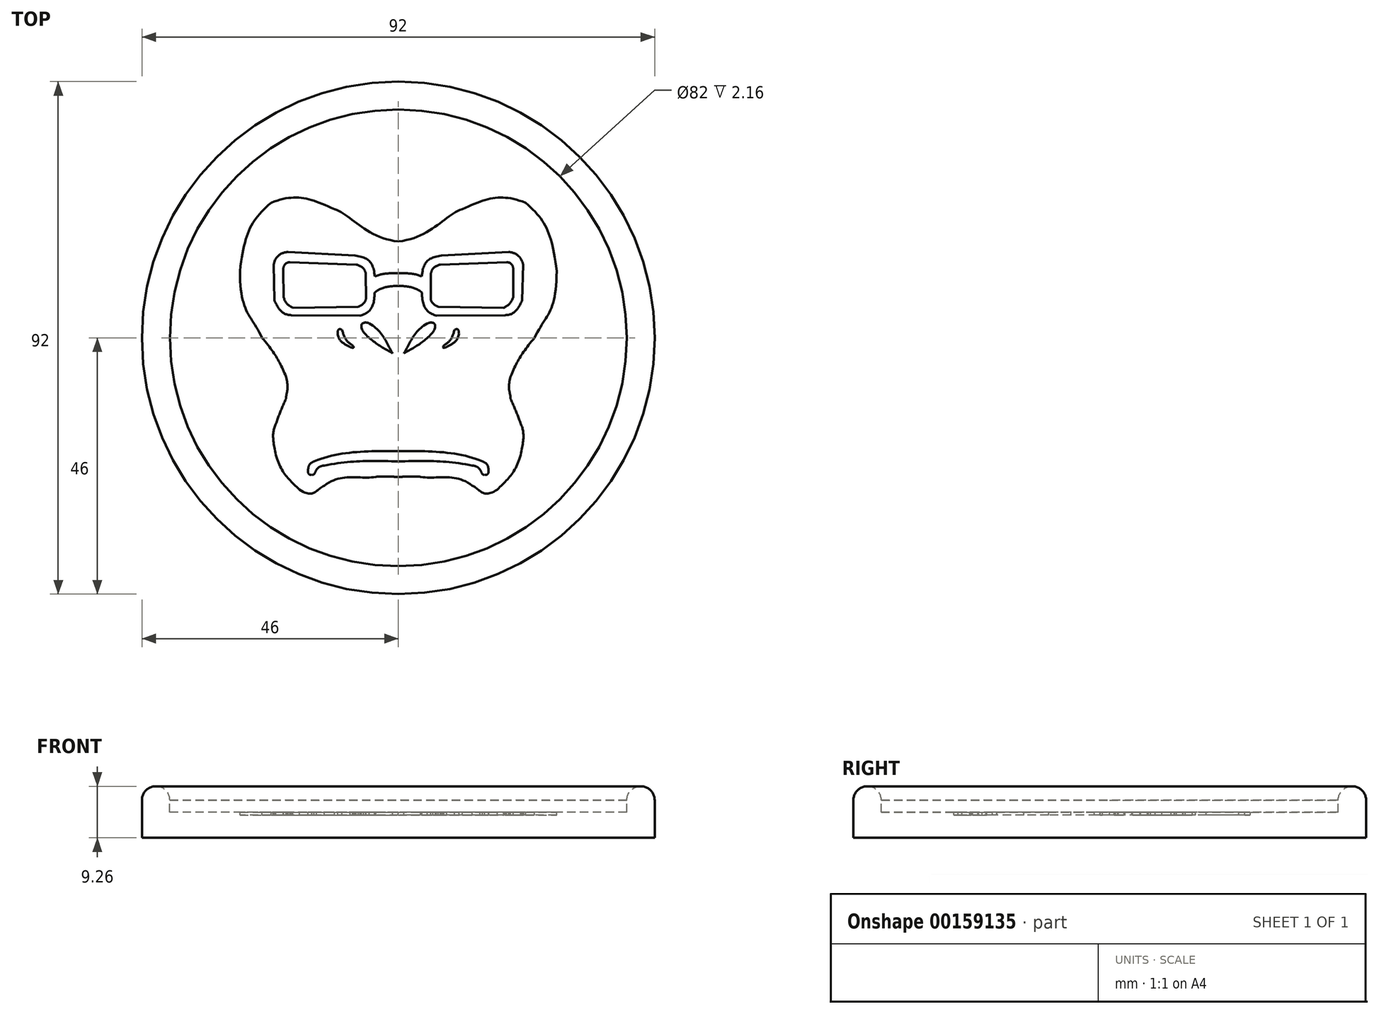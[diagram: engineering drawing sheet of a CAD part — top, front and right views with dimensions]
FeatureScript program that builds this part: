
annotation { "Feature Type Name" : "Feature", "Feature Type Description" : "" }
export const myFeature = defineFeature(function(context is Context, id is Id, definition is map)
    precondition{}
    {
        {
            var Q0;
            Q0=qCreatedBy(makeId("Top.planeOp"),FACE);
            var sketch = newSketch(context, id + "F0", { "sketchPlane" : qUnion([Q0])});
            skCircle(sketch, "E0", {"center": v(0, 0) * mm, "radius": 46 * mm});
            skSolve(sketch);
        }
        {
            var Q0;
            Q0 = qSketchRegion(id + "F0", true);
            extrude(context, id + "F1", {"entities" : qUnion([Q0]), "depth" : 4.6 * mm});
        }
        {
            var Q0;
            Q0=makeQuery(id+"F1.opExtrude","CAP_FACE",FACE,{"disambiguationData":[OSD([sQuery(id+"F0.wireOp",EDGE,"E0")])],"isStart":false});
            var sketch = newSketch(context, id + "F2", { "sketchPlane" : qUnion([Q0])});
            skCircle(sketch, "E1", {"center": v(0, 0) * mm, "radius": 41 * mm});
            skSolve(sketch);
        }
        {
            var Q0;
            Q0 = qSketchRegion(id + "F2", true);
            extrude(context, id + "F3", {"entities" : qUnion([Q0]), "operationType" : NewBodyOperationType.REMOVE, "oppositeDirection" : true, "depth" : 2.16 * mm});
        }
        {
            var Q0;
            Q0=makeQuery(id+"F3.boolean.opBoolean","COPY",FACE,{"derivedFrom":makeQuery(id+"F3.opExtrude","CAP_FACE",FACE,{"disambiguationData":[OSD([sQuery(id+"F2.wireOp",EDGE,"E1")])],"isStart":false})});
            var sketch = newSketch(context, id + "F4", { "sketchPlane" : qUnion([Q0])});
            skFitSpline(sketch, "E2", {"points": [v(-22.82, 24.26) * mm, v(-11.46, 23.12) * mm], "startDerivative": vector(13.27, 5.25) * mm, "endDerivative": vector(13.73, -6.02) * mm});
            skFitSpline(sketch, "E3", {"points": [v(-11.46, 23.12) * mm, v(0, 17.31) * mm], "startDerivative": vector(8.95, -2.93) * mm, "endDerivative": vector(17.4, -1.85) * mm});
            skFitSpline(sketch, "E4", {"points": [v(-22.82, 24.26) * mm, v(-28.41, 12) * mm], "startDerivative": vector(-11.27, -9.64) * mm, "endDerivative": vector(-2.55, -20.44) * mm});
            skFitSpline(sketch, "E5", {"points": [v(-28.41, 12) * mm, v(-24.46, 0) * mm], "startDerivative": vector(0, -22.56) * mm, "endDerivative": vector(6.05, -12.77) * mm});
            skFitSpline(sketch, "E6", {"points": [v(-24.46, 0) * mm, v(-20.15, -6.97) * mm], "startDerivative": vector(6.87, -7.99) * mm, "endDerivative": vector(3.27, -8.01) * mm});
            skFitSpline(sketch, "E7", {"points": [v(-20.15, -6.97) * mm, v(-20.15, -10.95) * mm], "startDerivative": vector(1.96, -7.52) * mm, "endDerivative": vector(0, -4.03) * mm});
            skFitSpline(sketch, "E8", {"points": [v(-20.15, -10.95) * mm, v(-21.95, -15.41) * mm], "startDerivative": vector(-2.02, -4.58) * mm, "endDerivative": vector(-1.63, -5.07) * mm});
            skFitSpline(sketch, "E9", {"points": [v(-21.95, -15.41) * mm, v(-21.95, -21.03) * mm], "startDerivative": vector(-2.13, -4.25) * mm, "endDerivative": vector(1.96, -8.66) * mm});
            skFitSpline(sketch, "E10", {"points": [v(-21.95, -21.03) * mm, v(-17.75, -27.24) * mm], "startDerivative": vector(2.29, -9) * mm, "endDerivative": vector(5.72, -5.56) * mm});
            skFitSpline(sketch, "E11", {"points": [v(-17.75, -27.24) * mm, v(-13.28, -26.53) * mm], "startDerivative": vector(8.01, -5.07) * mm, "endDerivative": vector(4.9, 2.29) * mm});
            skFitSpline(sketch, "E12", {"points": [v(-13.28, -26.53) * mm, v(-4.02, -24.95) * mm], "startDerivative": vector(9.65, 7.36) * mm, "endDerivative": vector(9.26, 1.58) * mm});
            skFitSpline(sketch, "E13", {"points": [v(-4.02, -24.95) * mm, v(0, -24.95) * mm], "startDerivative": vector(4.74, 0.5) * mm, "endDerivative": vector(4.02, 0) * mm});
            skLineSegment(sketch, "E14", {"start": v(0, -24.95) * mm, "end": v(0, 17.31) * mm});
            skFitSpline(sketch, "E15", {"points": [v(0, 11.64) * mm, v(-4.21, 11.03) * mm], "startDerivative": vector(-4.33, -0.13) * mm, "endDerivative": vector(-4.41, -1.82) * mm});
            skFitSpline(sketch, "E16", {"points": [v(-4.26, 8.14) * mm, v(0, 9.35) * mm], "startDerivative": vector(3.63, 2.98) * mm, "endDerivative": vector(5.11, 0.26) * mm});
            skFitSpline(sketch, "E17", {"points": [v(-4.26, 8.14) * mm, v(-6.85, 3.98) * mm], "startDerivative": vector(0, -7.66) * mm, "endDerivative": vector(-5.45, -1.56) * mm});
            skLineSegment(sketch, "E18", {"start": v(-19.18, 4.07) * mm, "end": v(-6.85, 3.98) * mm});
            skFitSpline(sketch, "E19", {"points": [v(-4.21, 11.03) * mm, v(-7.76, 14.8) * mm], "startDerivative": vector(-0.78, 7.79) * mm, "endDerivative": vector(-7.4, 1.17) * mm});
            skLineSegment(sketch, "E20", {"start": v(-19.78, 15.4) * mm, "end": v(-7.76, 14.8) * mm});
            skFitSpline(sketch, "E21", {"points": [v(-22.38, 13.11) * mm, v(-19.78, 15.4) * mm], "startDerivative": vector(1.04, 6.23) * mm, "endDerivative": vector(1.43, 0) * mm});
            skFitSpline(sketch, "E22", {"points": [v(-19.18, 4.07) * mm, v(-22.25, 6.8) * mm], "startDerivative": vector(-4.67, 0.26) * mm, "endDerivative": vector(-2.6, 5.84) * mm});
            skLineSegment(sketch, "E23", {"start": v(-22.38, 13.11) * mm, "end": v(-22.25, 6.8) * mm});
            skFitSpline(sketch, "E24", {"points": [v(-20.65, 12.12) * mm, v(-19.44, 13.59) * mm], "startDerivative": vector(0, 1.17) * mm, "endDerivative": vector(3.37, 0) * mm});
            skFitSpline(sketch, "E25", {"points": [v(-20.6, 7.32) * mm, v(-18.92, 5.41) * mm], "startDerivative": vector(1.43, -3.76) * mm, "endDerivative": vector(2.47, -1.3) * mm});
            skFitSpline(sketch, "E26", {"points": [v(-7.2, 5.59) * mm, v(-5.81, 6.97) * mm], "startDerivative": vector(1.95, 0.65) * mm, "endDerivative": vector(0.39, 2.08) * mm});
            skFitSpline(sketch, "E27", {"points": [v(-7.54, 13.15) * mm, v(-5.86, 11.6) * mm], "startDerivative": vector(3.63, -1.04) * mm, "endDerivative": vector(0.52, -2.2) * mm});
            skLineSegment(sketch, "E28", {"start": v(-19.44, 13.59) * mm, "end": v(-7.54, 13.15) * mm});
            skLineSegment(sketch, "E29", {"start": v(-5.81, 6.97) * mm, "end": v(-5.86, 11.6) * mm});
            skLineSegment(sketch, "E30", {"start": v(-7.2, 5.59) * mm, "end": v(-18.92, 5.41) * mm});
            skLineSegment(sketch, "E31", {"start": v(-20.6, 7.32) * mm, "end": v(-20.65, 12.12) * mm});
            skFitSpline(sketch, "E32", {"points": [v(-14.65, -23.65) * mm, v(-15.49, -24.62) * mm], "startDerivative": vector(-0.84, -0.97) * mm, "endDerivative": vector(-1.65, -0.1) * mm});
            skFitSpline(sketch, "E33", {"points": [v(-15.49, -24.62) * mm, v(-16.17, -23.55) * mm], "startDerivative": vector(-2.24, 0.1) * mm, "endDerivative": vector(0.2, 2.07) * mm});
            skFitSpline(sketch, "E34", {"points": [v(-16.17, -23.55) * mm, v(-15.1, -22.16) * mm], "startDerivative": vector(0.2, 3.01) * mm, "endDerivative": vector(1.56, 0.87) * mm});
            skFitSpline(sketch, "E35", {"points": [v(0, -20.31) * mm, v(-15.1, -22.16) * mm], "startDerivative": vector(-15.46, 0.1) * mm, "endDerivative": vector(-13.6, -5.64) * mm});
            skFitSpline(sketch, "E36", {"points": [v(-14.65, -23.65) * mm, v(-13.29, -22.9) * mm], "startDerivative": vector(0.87, 1.36) * mm, "endDerivative": vector(1.85, 0.2) * mm});
            skFitSpline(sketch, "E37", {"points": [v(-13.29, -22.9) * mm, v(0, -22.2) * mm], "startDerivative": vector(14.29, 2.72) * mm, "endDerivative": vector(14.29, -0.58) * mm});
            skFitSpline(sketch, "E38", {"points": [v(-10.9, 0.78) * mm, v(-8.67, -1.65) * mm], "startDerivative": vector(0.98, -5.13) * mm, "endDerivative": vector(3.27, -2.18) * mm});
            skFitSpline(sketch, "E39", {"points": [v(-10.9, 0.78) * mm, v(-10.1, 1.44) * mm], "startDerivative": vector(0.1, 2.5) * mm, "endDerivative": vector(1.53, -0.87) * mm});
            skFitSpline(sketch, "E40", {"points": [v(-10.1, 1.44) * mm, v(-8.2, -1.33) * mm], "startDerivative": vector(1.3, -4.31) * mm, "endDerivative": vector(3.82, -2.3) * mm});
            skFitSpline(sketch, "E41", {"points": [v(-8.67, -1.65) * mm, v(-8.2, -1.33) * mm], "startDerivative": vector(2.3, -0.87) * mm, "endDerivative": vector(-0.87, 0.98) * mm});
            skFitSpline(sketch, "E42", {"points": [v(-6.24, 1.04) * mm, v(-5.18, 2.56) * mm], "startDerivative": vector(-3.27, 5.24) * mm, "endDerivative": vector(1.96, -1.3) * mm});
            skFitSpline(sketch, "E43", {"points": [v(-5.18, 2.56) * mm, v(-1, -2.78) * mm], "startDerivative": vector(7.42, -3.93) * mm, "endDerivative": vector(3.06, -4.8) * mm});
            skFitSpline(sketch, "E44", {"points": [v(-6.24, 1.04) * mm, v(-1, -2.78) * mm], "startDerivative": vector(5.13, -5.78) * mm, "endDerivative": vector(5.46, -3.16) * mm});
            skFitSpline(sketch, "E45.MirrorCS", {"points": [v(4.21, 11.03) * mm, v(7.76, 14.8) * mm], "startDerivative": vector(0.78, 7.79) * mm, "endDerivative": vector(7.4, 1.17) * mm});
            skFitSpline(sketch, "E46.MirrorCS", {"points": [v(0, 11.64) * mm, v(4.21, 11.03) * mm], "startDerivative": vector(4.33, -0.13) * mm, "endDerivative": vector(4.41, -1.82) * mm});
            skFitSpline(sketch, "E47.MirrorCS", {"points": [v(4.26, 8.14) * mm, v(0, 9.35) * mm], "startDerivative": vector(-3.63, 2.98) * mm, "endDerivative": vector(-5.11, 0.26) * mm});
            skLineSegment(sketch, "E48.MirrorCS", {"start": v(19.78, 15.4) * mm, "end": v(7.76, 14.8) * mm});
            skFitSpline(sketch, "E49.MirrorCS", {"points": [v(22.38, 13.11) * mm, v(19.78, 15.4) * mm], "startDerivative": vector(-1.04, 6.23) * mm, "endDerivative": vector(-1.43, 0) * mm});
            skFitSpline(sketch, "E50.MirrorCS", {"points": [v(19.18, 4.07) * mm, v(22.25, 6.8) * mm], "startDerivative": vector(4.67, 0.26) * mm, "endDerivative": vector(2.6, 5.84) * mm});
            skLineSegment(sketch, "E51.MirrorCS", {"start": v(19.18, 4.07) * mm, "end": v(6.85, 3.98) * mm});
            skLineSegment(sketch, "E52.MirrorCS", {"start": v(22.38, 13.11) * mm, "end": v(22.25, 6.8) * mm});
            skFitSpline(sketch, "E53.MirrorCS", {"points": [v(4.26, 8.14) * mm, v(6.85, 3.98) * mm], "startDerivative": vector(0, -7.66) * mm, "endDerivative": vector(5.45, -1.56) * mm});
            skLineSegment(sketch, "E54.MirrorCS", {"start": v(19.44, 13.59) * mm, "end": v(7.54, 13.15) * mm});
            skFitSpline(sketch, "E55.MirrorCS", {"points": [v(7.54, 13.15) * mm, v(5.86, 11.6) * mm], "startDerivative": vector(-3.63, -1.04) * mm, "endDerivative": vector(-0.52, -2.2) * mm});
            skLineSegment(sketch, "E56.MirrorCS", {"start": v(5.81, 6.97) * mm, "end": v(5.86, 11.6) * mm});
            skLineSegment(sketch, "E57.MirrorCS", {"start": v(7.2, 5.59) * mm, "end": v(18.92, 5.41) * mm});
            skLineSegment(sketch, "E58.MirrorCS", {"start": v(20.6, 7.32) * mm, "end": v(20.65, 12.12) * mm});
            skFitSpline(sketch, "E59.MirrorCS", {"points": [v(20.6, 7.32) * mm, v(18.92, 5.41) * mm], "startDerivative": vector(-1.43, -3.76) * mm, "endDerivative": vector(-2.47, -1.3) * mm});
            skFitSpline(sketch, "E60.MirrorCS", {"points": [v(7.2, 5.59) * mm, v(5.81, 6.97) * mm], "startDerivative": vector(-1.95, 0.65) * mm, "endDerivative": vector(-0.39, 2.08) * mm});
            skFitSpline(sketch, "E61.MirrorCS", {"points": [v(20.65, 12.12) * mm, v(19.44, 13.59) * mm], "startDerivative": vector(0, 1.17) * mm, "endDerivative": vector(-3.37, 0) * mm});
            skFitSpline(sketch, "E62.MirrorCS", {"points": [v(6.24, 1.04) * mm, v(5.18, 2.56) * mm], "startDerivative": vector(3.27, 5.24) * mm, "endDerivative": vector(-1.96, -1.3) * mm});
            skFitSpline(sketch, "E63.MirrorCS", {"points": [v(5.18, 2.56) * mm, v(1, -2.78) * mm], "startDerivative": vector(-7.42, -3.93) * mm, "endDerivative": vector(-3.06, -4.8) * mm});
            skFitSpline(sketch, "E64.MirrorCS", {"points": [v(6.24, 1.04) * mm, v(1, -2.78) * mm], "startDerivative": vector(-5.13, -5.78) * mm, "endDerivative": vector(-5.46, -3.16) * mm});
            skFitSpline(sketch, "E65.MirrorCS", {"points": [v(10.9, 0.78) * mm, v(10.1, 1.44) * mm], "startDerivative": vector(-0.1, 2.5) * mm, "endDerivative": vector(-1.53, -0.87) * mm});
            skFitSpline(sketch, "E66.MirrorCS", {"points": [v(10.9, 0.78) * mm, v(8.67, -1.65) * mm], "startDerivative": vector(-0.98, -5.13) * mm, "endDerivative": vector(-3.27, -2.18) * mm});
            skFitSpline(sketch, "E67.MirrorCS", {"points": [v(10.1, 1.44) * mm, v(8.2, -1.33) * mm], "startDerivative": vector(-1.3, -4.31) * mm, "endDerivative": vector(-3.82, -2.3) * mm});
            skFitSpline(sketch, "E68.MirrorCS", {"points": [v(8.67, -1.65) * mm, v(8.2, -1.33) * mm], "startDerivative": vector(-2.3, -0.87) * mm, "endDerivative": vector(0.87, 0.98) * mm});
            skFitSpline(sketch, "E69.MirrorCS", {"points": [v(22.82, 24.26) * mm, v(11.46, 23.12) * mm], "startDerivative": vector(-13.27, 5.25) * mm, "endDerivative": vector(-13.73, -6.02) * mm});
            skFitSpline(sketch, "E70.MirrorCS", {"points": [v(22.82, 24.26) * mm, v(28.41, 12) * mm], "startDerivative": vector(11.27, -9.64) * mm, "endDerivative": vector(2.55, -20.44) * mm});
            skFitSpline(sketch, "E71.MirrorCS", {"points": [v(11.46, 23.12) * mm, v(0, 17.31) * mm], "startDerivative": vector(-8.95, -2.93) * mm, "endDerivative": vector(-17.4, -1.85) * mm});
            skFitSpline(sketch, "E72.MirrorCS", {"points": [v(28.41, 12) * mm, v(24.46, 0) * mm], "startDerivative": vector(0, -22.56) * mm, "endDerivative": vector(-6.05, -12.77) * mm});
            skFitSpline(sketch, "E73.MirrorCS", {"points": [v(24.46, 0) * mm, v(20.15, -6.97) * mm], "startDerivative": vector(-6.87, -7.99) * mm, "endDerivative": vector(-3.27, -8.01) * mm});
            skFitSpline(sketch, "E74.MirrorCS", {"points": [v(20.15, -6.97) * mm, v(20.15, -10.95) * mm], "startDerivative": vector(-1.96, -7.52) * mm, "endDerivative": vector(0, -4.03) * mm});
            skFitSpline(sketch, "E75.MirrorCS", {"points": [v(20.15, -10.95) * mm, v(21.95, -15.41) * mm], "startDerivative": vector(2.02, -4.58) * mm, "endDerivative": vector(1.63, -5.07) * mm});
            skFitSpline(sketch, "E76.MirrorCS", {"points": [v(21.95, -15.41) * mm, v(21.95, -21.03) * mm], "startDerivative": vector(2.13, -4.25) * mm, "endDerivative": vector(-1.96, -8.66) * mm});
            skFitSpline(sketch, "E77.MirrorCS", {"points": [v(21.95, -21.03) * mm, v(17.75, -27.24) * mm], "startDerivative": vector(-2.29, -9) * mm, "endDerivative": vector(-5.72, -5.56) * mm});
            skFitSpline(sketch, "E78.MirrorCS", {"points": [v(17.75, -27.24) * mm, v(13.28, -26.53) * mm], "startDerivative": vector(-8.01, -5.07) * mm, "endDerivative": vector(-4.9, 2.29) * mm});
            skFitSpline(sketch, "E79.MirrorCS", {"points": [v(13.28, -26.53) * mm, v(4.02, -24.95) * mm], "startDerivative": vector(-9.65, 7.36) * mm, "endDerivative": vector(-9.26, 1.58) * mm});
            skFitSpline(sketch, "E80.MirrorCS", {"points": [v(4.02, -24.95) * mm, v(0, -24.95) * mm], "startDerivative": vector(-4.74, 0.5) * mm, "endDerivative": vector(-4.02, 0) * mm});
            skFitSpline(sketch, "E81.MirrorCS", {"points": [v(13.29, -22.9) * mm, v(0, -22.2) * mm], "startDerivative": vector(-14.29, 2.72) * mm, "endDerivative": vector(-14.29, -0.58) * mm});
            skFitSpline(sketch, "E82.MirrorCS", {"points": [v(0, -20.31) * mm, v(15.1, -22.16) * mm], "startDerivative": vector(15.46, 0.1) * mm, "endDerivative": vector(13.6, -5.64) * mm});
            skFitSpline(sketch, "E83.MirrorCS", {"points": [v(16.17, -23.55) * mm, v(15.1, -22.16) * mm], "startDerivative": vector(-0.2, 3.01) * mm, "endDerivative": vector(-1.56, 0.87) * mm});
            skFitSpline(sketch, "E84.MirrorCS", {"points": [v(15.49, -24.62) * mm, v(16.17, -23.55) * mm], "startDerivative": vector(2.24, 0.1) * mm, "endDerivative": vector(-0.2, 2.07) * mm});
            skFitSpline(sketch, "E85.MirrorCS", {"points": [v(14.65, -23.65) * mm, v(15.49, -24.62) * mm], "startDerivative": vector(0.84, -0.97) * mm, "endDerivative": vector(1.65, -0.1) * mm});
            skFitSpline(sketch, "E86.MirrorCS", {"points": [v(14.65, -23.65) * mm, v(13.29, -22.9) * mm], "startDerivative": vector(-0.87, 1.36) * mm, "endDerivative": vector(-1.85, 0.2) * mm});
            skSolve(sketch);
        }
        {
            var Q0;
            Q0 = qSketchRegion(id + "F4", true);
            var Q1;
            Q1=makeQuery(id+"F4.imprint","IMPRINT",FACE,{"disambiguationData":[TD([[makeQuery(id+"F4.imprint","IMPRINT",EDGE,{"derivedFrom":sQuery(id+"F4.wireOp",EDGE,"E24")}),-1.0]])]});
            var Q2;
            Q2=makeQuery(id+"F4.imprint","IMPRINT",FACE,{"disambiguationData":[TD([[makeQuery(id+"F4.imprint","IMPRINT",EDGE,{"derivedFrom":sQuery(id+"F4.wireOp",EDGE,"E54.MirrorCS")}),1.0]])]});
            extrude(context, id + "F5", {"entities" : qUnion([Q0, Q1, Q2]), "operationType" : NewBodyOperationType.REMOVE, "oppositeDirection" : true, "depth" : .5 * mm});
        }
        {
            var Q0;
            Q0=makeQuery(id+"F1.opExtrude","CAP_FACE",FACE,{"disambiguationData":[OSD([sQuery(id+"F0.wireOp",EDGE,"E0")])],"isStart":true});
            var sketch = newSketch(context, id + "F6", { "sketchPlane" : qUnion([Q0])});
            skCircle(sketch, "E87", {"center": v(0, 0) * mm, "radius": 46 * mm});
            skSolve(sketch);
        }
        {
            var Q0;
            Q0 = qSketchRegion(id + "F6", true);
            extrude(context, id + "F7", {"entities" : qUnion([Q0]), "operationType" : NewBodyOperationType.ADD, "depth" : 2.16 * mm});
        }
        {
            var Q0;
            Q0=qCreatedBy(makeId("Front.planeOp"),FACE);
            var sketch = newSketch(context, id + "F8", { "sketchPlane" : qUnion([Q0])});
            skLineSegment(sketch, "E88", {"start": v(46, 4.6) * mm, "end": v(46, -2.16) * mm});
            skPoint(sketch, "E89.start.orphan", {"position": v(-41.5, 0) * mm});
            skLineSegment(sketch, "E90", {"start": v(-46, 4.6) * mm, "end": v(-41, 4.6) * mm});
            skLineSegment(sketch, "E91", {"start": v(0, 0) * mm, "end": v(0, 9.05) * mm});
            skLineSegment(sketch, "E92", {"start": v(0, 0) * mm, "end": v(-41, 0) * mm});
            skLineSegment(sketch, "E93", {"start": v(-41, 0) * mm, "end": v(-41, 4.6) * mm});
            skArc(sketch, "E94", {"start": v(-41, 4.6) * mm, "mid": v(-43.5, 7.1) * mm, "end": v(-46, 4.6) * mm});
            skSolve(sketch);
        }
        {
            var Q0;
            Q0 = qSketchRegion(id + "F8", true);
            var Q1;
            Q1=sQuery(id+"F8.wireOp",EDGE,"E91");
            revolve(context, id + "F9", {"operationType" : NewBodyOperationType.ADD, "entities" : qUnion([Q0]), "axis" : qUnion([Q1]), "revolveType" : RevolveType.FULL});
        }
    });
